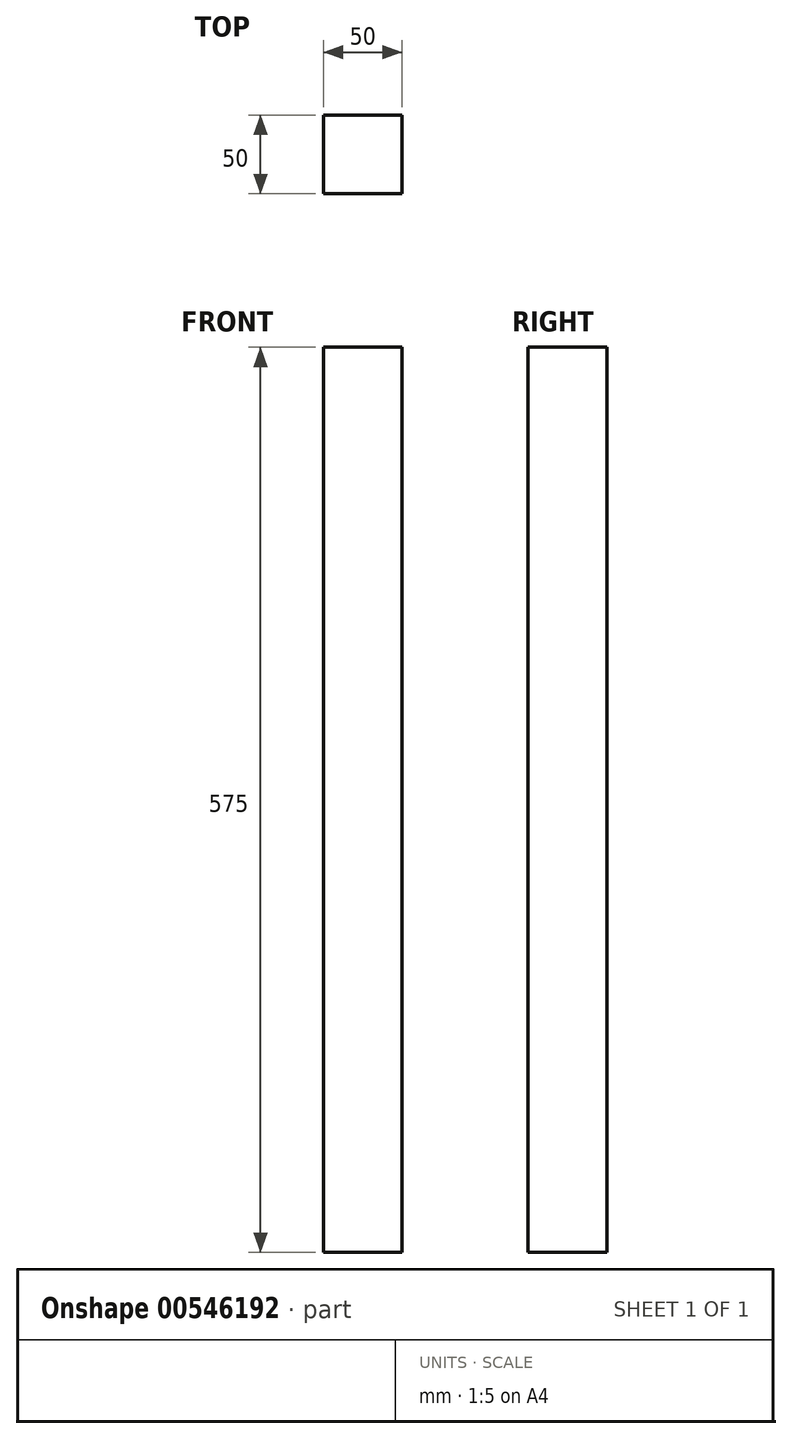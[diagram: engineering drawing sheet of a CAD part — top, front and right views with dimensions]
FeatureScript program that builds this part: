
annotation { "Feature Type Name" : "Feature", "Feature Type Description" : "" }
export const myFeature = defineFeature(function(context is Context, id is Id, definition is map)
    precondition{}
    {
        {
            var Q0;
            Q0=qCreatedBy(makeId("Top.planeOp"),FACE);
            var sketch = newSketch(context, id + "F0", { "sketchPlane" : qUnion([Q0])});
            skLineSegment(sketch, "E0.bottom", {"start": v(0, 0) * mm, "end": v(50, 0) * mm});
            skLineSegment(sketch, "E0.top", {"start": v(0, 50) * mm, "end": v(50, 50) * mm});
            skLineSegment(sketch, "E0.left", {"start": v(0, 0) * mm, "end": v(0, 50) * mm});
            skLineSegment(sketch, "E0.right", {"start": v(50, 0) * mm, "end": v(50, 50) * mm});
            skSolve(sketch);
        }
        {
            var Q0;
            Q0 = qSketchRegion(id + "F0", true);
            extrude(context, id + "F1", {"entities" : qUnion([Q0]), "depth" : 575 * mm, "offsetDistance" : 25 * mm});
        }
    });
